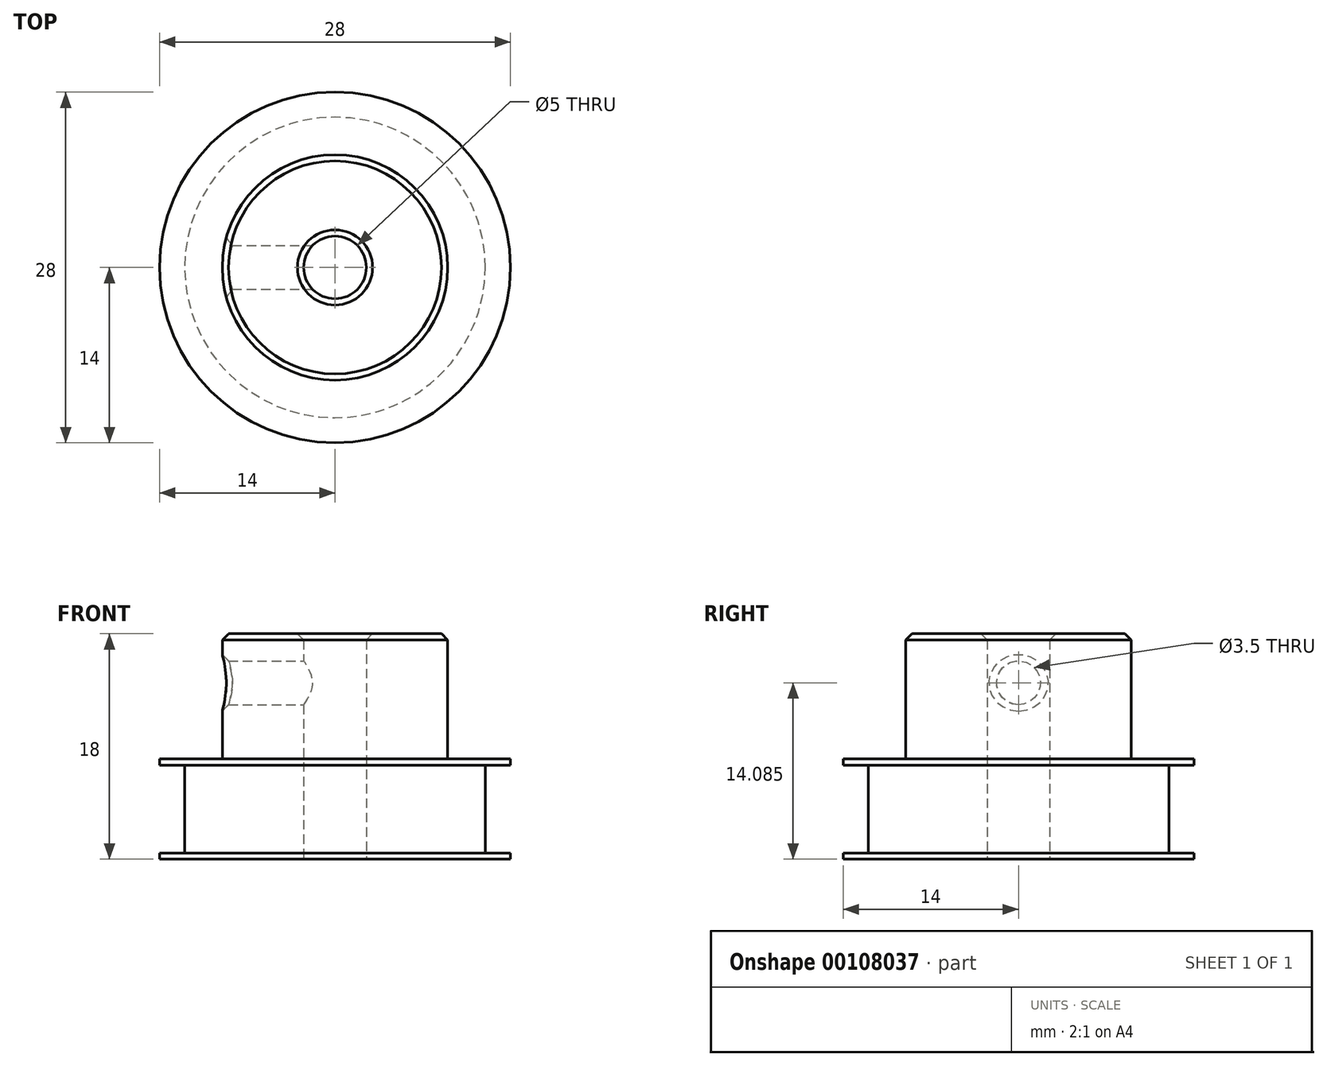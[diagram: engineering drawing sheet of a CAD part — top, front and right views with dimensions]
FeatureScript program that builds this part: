
annotation { "Feature Type Name" : "Feature", "Feature Type Description" : "" }
export const myFeature = defineFeature(function(context is Context, id is Id, definition is map)
    precondition{}
    {
        {
            var Q0;
            Q0=qCreatedBy(makeId("Front.planeOp"),FACE);
            var sketch = newSketch(context, id + "F0", { "sketchPlane" : qUnion([Q0])});
            skLineSegment(sketch, "E0", {"start": v(0, 0) * mm, "end": v(0, 8) * mm, "construction": true});
            skLineSegment(sketch, "E1", {"start": v(9, 8) * mm, "end": v(14, 8) * mm});
            skLineSegment(sketch, "E2", {"start": v(14, 8) * mm, "end": v(14, 7.5) * mm});
            skLineSegment(sketch, "E3", {"start": v(14, 7.5) * mm, "end": v(12, 7.5) * mm});
            skLineSegment(sketch, "E4", {"start": v(12, 7.5) * mm, "end": v(12, 0.5) * mm});
            skLineSegment(sketch, "E5", {"start": v(12, 0.5) * mm, "end": v(14, 0.5) * mm});
            skLineSegment(sketch, "E6", {"start": v(14, 0.5) * mm, "end": v(14, 0) * mm});
            skLineSegment(sketch, "E7", {"start": v(14, 0) * mm, "end": v(0, 0) * mm});
            skLineSegment(sketch, "E8", {"start": v(9, 8) * mm, "end": v(9, 18) * mm});
            skLineSegment(sketch, "E9", {"start": v(9, 18) * mm, "end": v(0, 18) * mm});
            skLineSegment(sketch, "E10", {"start": v(0, 18) * mm, "end": v(0, 0) * mm});
            skSolve(sketch);
        }
        {
            var Q0;
            Q0 = qSketchRegion(id + "F0", true);
            var Q1;
            Q1=sQuery(id+"F0.wireOp",EDGE,"E10");
            revolve(context, id + "F1", {"entities" : qUnion([Q0]), "axis" : qUnion([Q1]), "revolveType" : RevolveType.FULL});
        }
        {
            var Q0;
            Q0=makeQuery(id+"F1.opRevolve","SWEPT_FACE",FACE,{"disambiguationData":[OSD([sQuery(id+"F0.wireOp",EDGE,"E7")])]});
            var sketch = newSketch(context, id + "F2", { "sketchPlane" : qUnion([Q0])});
            skCircle(sketch, "E11", {"center": v(0, 0) * mm, "radius": 2.5 * mm});
            skSolve(sketch);
        }
        {
            var Q0;
            Q0 = qSketchRegion(id + "F2", true);
            extrude(context, id + "F3", {"entities" : qUnion([Q0]), "operationType" : NewBodyOperationType.REMOVE, "endBound" : BoundingType.THROUGH_ALL, "oppositeDirection" : true, "depth" : 25 * mm});
        }
        {
            var Q0;
            Q0=makeQuery(id+"F3.boolean.opBoolean","COPY",EDGE,{"derivedFrom":makeQuery(id+"F3.opExtrude","CAP_EDGE",EDGE,{"disambiguationData":[OSD([sQuery(id+"F2.wireOp",EDGE,"E11")])],"isStart":true})});
            var Q1;
            Q1=makeQuery(id+"F3.boolean.opBoolean","INTERSECT",EDGE,{"derivedFrom":[makeQuery(id+"F1.opRevolve","SWEPT_FACE",FACE,{"disambiguationData":[OSD([sQuery(id+"F0.wireOp",EDGE,"E9")])]}),makeQuery(id+"F3.opExtrude","SWEPT_FACE",FACE,{"disambiguationData":[OSD([sQuery(id+"F2.wireOp",EDGE,"E11")])]})]});
            chamfer(context, id + "F4", {"entities" : qUnion([Q0, Q1]), "width" : 0.5 * mm, "tangentPropagation" : true});
        }
        {
            var Q0;
            Q0=makeQuery(id+"F1.opRevolve","SWEPT_EDGE",EDGE,{"disambiguationData":[OSD([sQuery(id+"F0.wireOp",EDGE,"E8"),sQuery(id+"F0.wireOp",EDGE,"E9")])]});
            chamfer(context, id + "F5", {"entities" : qUnion([Q0]), "width" : 0.5 * mm, "tangentPropagation" : true});
        }
        {
            var Q0;
            Q0=qCreatedBy(makeId("Right.planeOp"),FACE);
            var sketch = newSketch(context, id + "F6", { "sketchPlane" : qUnion([Q0])});
            skCircle(sketch, "E12", {"center": v(0, 14.08) * mm, "radius": 1.75 * mm});
            skSolve(sketch);
        }
        {
            var Q0;
            Q0 = qSketchRegion(id + "F6", true);
            extrude(context, id + "F7", {"entities" : qUnion([Q0]), "operationType" : NewBodyOperationType.REMOVE, "oppositeDirection" : true, "depth" : 25 * mm});
        }
        {
            var Q0;
            Q0=makeQuery(id+"F7.boolean.opBoolean","INTERSECT",EDGE,{"derivedFrom":[makeQuery(id+"F1.opRevolve","SWEPT_FACE",FACE,{"disambiguationData":[OSD([sQuery(id+"F0.wireOp",EDGE,"E8")])]}),makeQuery(id+"F7.opExtrude","SWEPT_FACE",FACE,{"disambiguationData":[OSD([sQuery(id+"F6.wireOp",EDGE,"E12")])]})]});
            chamfer(context, id + "F8", {"entities" : qUnion([Q0]), "width" : 0.5 * mm, "tangentPropagation" : true});
        }
    });
